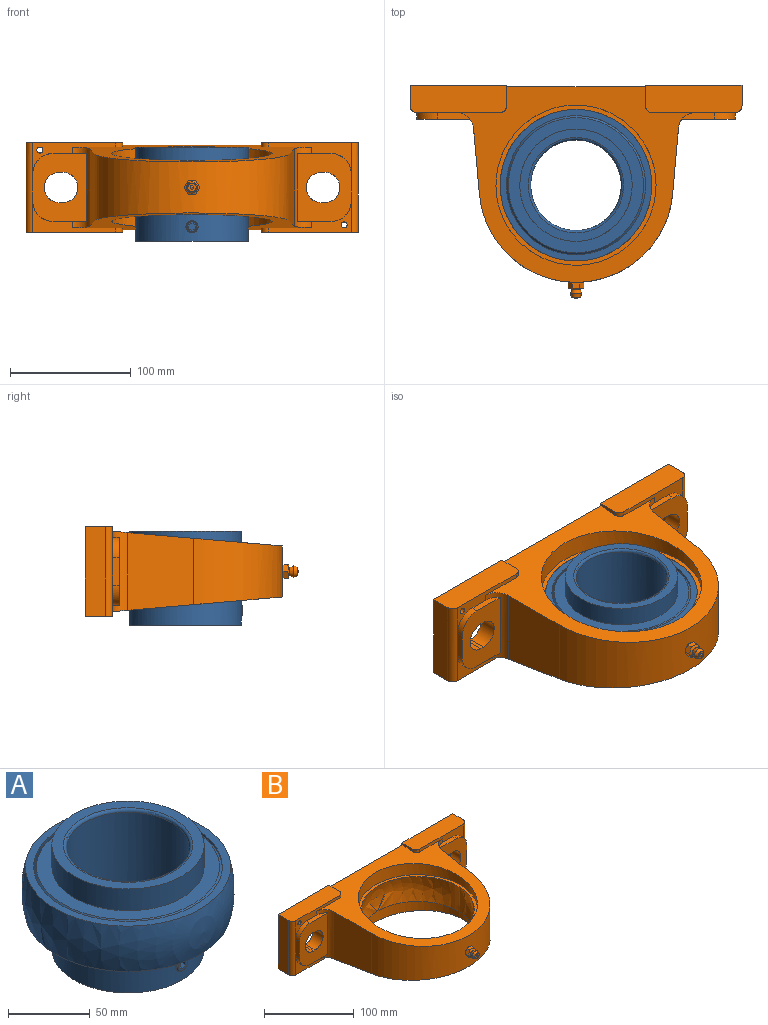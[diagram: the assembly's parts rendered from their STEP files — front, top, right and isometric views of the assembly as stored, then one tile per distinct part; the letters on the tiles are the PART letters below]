
ASSEMBLY  parts=2 mates=1
PART A: 143 faces, bbox 127.1x129.4x131.6 mm
  f0: plane 7.1x6.16mm, normal (0.87,0.5,0), area 38.5mm2, adj f1
  f1: cone r=1.71mm half-angle=45deg, axis (0.87,0.5,0), area 56.6mm2, adj f0,f2
  f2: cylinder r=5mm len=10.05mm, axis (0.87,0.5,0), area 79.3mm2, adj f1,f3
  f3: cylinder r=37.5mm len=75mm, axis (0,0,1), area 17220.6mm2, adj f2,f4,f139,f142
  f4: torus R=39.5mm, axis (0,0,-1), area 754.6mm2, adj f3,f5
  f5: plane 93.01x93.01mm, normal (0,0,-1), area 1887mm2, adj f4,f6
  f6: cylinder r=46.5mm len=93mm, axis (0,0,-1), area 7783.3mm2, adj f5,f7,f105,f106,f107,f108,f109,f110
  f7: sphere r=8.34mm, area 847.9mm2, adj f6,f8,f9,f10,f53,f54,f55,f56
  f8: torus R=51.49mm, axis (0,0,1), area 160.7mm2, adj f7,f9,f95,f106
  f9: torus R=51.49mm, axis (0,0,1), area 160.7mm2, adj f7,f8,f10,f106
  f10: cylinder r=56.49mm len=112.98mm, axis (0,0,1), area 2460.6mm2, adj f7,f9,f11,f13,f15,f17,f19,f21
  f11: torus R=51.49mm, axis (0,0,1), area 160.8mm2, adj f10,f12,f118,f120
  f12: torus R=51.49mm, axis (0,0,1), area 160.7mm2, adj f11,f95,f118,f120
  f13: torus R=51.49mm, axis (0,0,1), area 160.7mm2, adj f10,f14,f116,f118
  f14: torus R=51.49mm, axis (0,0,1), area 160.7mm2, adj f13,f95,f116,f118
  f15: torus R=51.49mm, axis (0,0,1), area 160.7mm2, adj f10,f16,f114,f116
  f16: torus R=51.49mm, axis (0,0,1), area 160.7mm2, adj f15,f95,f114,f116
  f17: torus R=51.49mm, axis (0,0,1), area 160.7mm2, adj f10,f18,f112,f114
  f18: torus R=51.49mm, axis (0,0,1), area 160.7mm2, adj f17,f95,f112,f114
  f19: torus R=51.49mm, axis (0,0,1), area 160.7mm2, adj f10,f20,f110,f112
  f20: torus R=51.49mm, axis (0,0,1), area 160.7mm2, adj f19,f95,f110,f112
  f21: torus R=51.49mm, axis (0,0,1), area 81.7mm2, adj f10,f22,f24,f110
  f22: torus R=51.49mm, axis (0,0,1), area 81.7mm2, adj f21,f23,f95,f110
  f23: torus R=51.49mm, axis (0,0,1), area 78.9mm2, adj f22,f24,f95,f108
  f24: torus R=51.49mm, axis (0,0,1), area 79mm2, adj f10,f21,f23,f108
  f25: torus R=51.49mm, axis (0,0,1), area 160.7mm2, adj f10,f26,f106,f108
  f26: torus R=51.49mm, axis (0,0,1), area 160.7mm2, adj f25,f95,f106,f108
  f27: torus R=51.49mm, axis (0,0,1), area 160.7mm2, adj f10,f28,f135,f137
  f28: torus R=51.49mm, axis (0,0,1), area 160.7mm2, adj f27,f95,f135,f137
  f29: torus R=51.49mm, axis (0,0,1), area 160.7mm2, adj f10,f30,f133,f135
  f30: torus R=51.49mm, axis (0,0,1), area 160.7mm2, adj f29,f95,f133,f135
  f31: torus R=51.49mm, axis (0,0,1), area 160.7mm2, adj f10,f32,f131,f133
  f32: torus R=51.49mm, axis (0,0,1), area 160.7mm2, adj f31,f95,f131,f133
  f33: torus R=51.49mm, axis (0,0,1), area 160.7mm2, adj f10,f34,f129,f131
  f34: torus R=51.49mm, axis (0,0,1), area 160.7mm2, adj f33,f95,f129,f131
  f35: torus R=51.49mm, axis (0,0,1), area 160.7mm2, adj f10,f36,f127,f129
  f36: torus R=51.49mm, axis (0,0,1), area 160.7mm2, adj f35,f95,f127,f129
  f37: torus R=51.49mm, axis (0,0,1), area 160.7mm2, adj f10,f38,f124,f127
  f38: torus R=51.49mm, axis (0,0,1), area 160.7mm2, adj f37,f95,f124,f127
  f39: torus R=51.49mm, axis (0,0,1), area 160.8mm2, adj f10,f40,f122,f124
  f40: torus R=51.49mm, axis (0,0,1), area 160.7mm2, adj f39,f95,f122,f124
  f41: torus R=51.49mm, axis (0,0,1), area 160.8mm2, adj f10,f42,f120,f122
  f42: torus R=51.49mm, axis (0,0,1), area 160.7mm2, adj f41,f95,f120,f122
  f43: cylinder r=0.87mm len=9.02mm, axis (0,-0.97,0.26), area 45.2mm2, adj f10,f44
  f44: sphere r=65mm, area 19597mm2, adj f43,f45
  f45: plane 125.48x125.48mm, normal (0,0,1), area 1907.7mm2, adj f44,f46
  f46: cylinder r=57.62mm len=115.24mm, axis (0,0,1), area 611.8mm2, adj f45,f47
  f47: cone r=55.93mm half-angle=45deg, axis (0,0,1), area 852.6mm2, adj f46,f48
  f48: plane 113.5x113.5mm, normal (0,0,1), area 3025.4mm2, adj f47,f49
  f49: cylinder r=46.51mm len=93.02mm, axis (0,0,-1), area 990.7mm2, adj f48,f50
  f50: plane 115.25x115.25mm, normal (0,0,-1), area 3627.1mm2, adj f49,f51
  f51: cylinder r=57.62mm len=115.24mm, axis (0,0,1), area 3.6mm2, adj f50,f52
  f52: plane 115.25x115.25mm, normal (0,0,1), area 412mm2, adj f10,f51
  f53: torus R=51.49mm, axis (0,0,1), area 160.7mm2, adj f7,f10,f54,f137
  f54: torus R=51.49mm, axis (0,0,1), area 160.7mm2, adj f7,f53,f95,f137
  f55: torus R=51.49mm, axis (0,0,1), area 120.6mm2, adj f7,f56,f137,f138
  f56: cylinder r=46.5mm len=93mm, axis (0,0,-1), area 10888.8mm2, adj f7,f55,f57,f67,f68,f69,f70,f71
  f57: cylinder r=5mm len=10mm, axis (-0.87,-0.5,0), area 4.9mm2, adj f56,f58
  f58: cone r=2.14mm half-angle=45deg, axis (-0.87,-0.5,0), area 37.1mm2, adj f57,f59
  f59: plane 8.28x7.19mm, normal (-0.87,-0.5,0), area 30.7mm2, adj f58,f60,f62,f63,f64,f65,f66
  f60: plane 5.58x4.67mm, normal (-0.25,0.43,0.87), area 14.4mm2, adj f59,f61,f62,f66
  f61: plane 5.77x4.33mm, normal (-0.87,-0.5,0), area 21.7mm2, adj f60,f62,f63,f64,f65,f66
  f62: plane 5.58x4.67mm, normal (0.25,-0.43,0.87), area 14.4mm2, adj f59,f60,f61,f63
  f63: plane 4.33x2.89mm, normal (0.5,-0.87,0), area 14.4mm2, adj f59,f61,f62,f64
  f64: plane 5.58x4.67mm, normal (0.25,-0.43,-0.87), area 14.4mm2, adj f59,f61,f63,f65
  f65: plane 5.58x4.67mm, normal (-0.25,0.43,-0.87), area 14.4mm2, adj f59,f61,f64,f66
  f66: plane 4.33x2.89mm, normal (-0.5,0.87,0), area 14.4mm2, adj f59,f60,f61,f65
  f67: torus R=51.49mm, axis (0,0,1), area 120.6mm2, adj f56,f118,f119,f120
  f68: torus R=51.49mm, axis (0,0,1), area 120.6mm2, adj f56,f116,f117,f118
  f69: torus R=51.49mm, axis (0,0,1), area 120.6mm2, adj f56,f114,f115,f116
  f70: torus R=51.49mm, axis (0,0,1), area 120.6mm2, adj f56,f112,f113,f114
  f71: torus R=51.49mm, axis (0,0,1), area 120.6mm2, adj f56,f110,f111,f112
  f72: torus R=51.49mm, axis (0,0,1), area 120.6mm2, adj f56,f108,f109,f110
  f73: torus R=51.49mm, axis (0,0,1), area 120.6mm2, adj f56,f106,f107,f108
  f74: torus R=51.49mm, axis (0,0,1), area 120.6mm2, adj f56,f135,f136,f137
  f75: torus R=51.49mm, axis (0,0,1), area 120.6mm2, adj f56,f133,f134,f135
  f76: torus R=51.49mm, axis (0,0,1), area 120.6mm2, adj f56,f131,f132,f133
  f77: torus R=51.49mm, axis (0,0,1), area 120.6mm2, adj f56,f129,f130,f131
  f78: torus R=51.49mm, axis (0,0,1), area 120.6mm2, adj f56,f127,f128,f129
  f79: torus R=51.49mm, axis (0,0,1), area 59.1mm2, adj f56,f80,f126,f127
  f80: torus R=51.49mm, axis (0,0,1), area 61.5mm2, adj f56,f79,f124,f125
  f81: torus R=51.49mm, axis (0,0,1), area 120.6mm2, adj f56,f122,f123,f124
  f82: torus R=51.49mm, axis (0,0,1), area 120.6mm2, adj f56,f120,f121,f122
  f83: plane 93.01x93.01mm, normal (0,0,1), area 1887mm2, adj f56,f142
  f84: cylinder r=5mm len=10mm, axis (0,1,0), area 4.9mm2, adj f56,f85
  f85: cone r=4.08mm half-angle=45deg, axis (0,1,0), area 37.1mm2, adj f84,f86
  f86: plane 8.28x8.28mm, normal (0,1,0), area 30.7mm2, adj f85,f87,f89,f90,f91,f92,f93
  f87: plane 5x2.5mm, normal (0.5,0,0.87), area 14.4mm2, adj f86,f88,f89,f93
  f88: plane 5.77x5mm, normal (0,1,0), area 21.7mm2, adj f87,f89,f90,f91,f92,f93
  f89: plane 5x2.5mm, normal (-0.5,0,0.87), area 14.4mm2, adj f86,f87,f88,f90
  f90: plane 5x2.89mm, normal (-1,0,0), area 14.4mm2, adj f86,f88,f89,f91
  f91: plane 5x2.5mm, normal (-0.5,0,-0.87), area 14.4mm2, adj f86,f88,f90,f92
  f92: plane 5x2.5mm, normal (0.5,0,-0.87), area 14.4mm2, adj f86,f88,f91,f93
  f93: plane 5x2.89mm, normal (1,0,0), area 14.4mm2, adj f86,f87,f88,f92
  f94: torus R=51.49mm, axis (0,0,1), area 120.6mm2, adj f7,f56,f105,f106
  f95: cylinder r=56.49mm len=112.98mm, axis (0,0,1), area 2463.2mm2, adj f7,f8,f12,f14,f16,f18,f20,f22
  f96: plane 115.25x115.25mm, normal (0,0,-1), area 397.7mm2, adj f95,f97
  f97: cylinder r=57.62mm len=115.24mm, axis (0,0,1), area 3.6mm2, adj f96,f98
  f98: plane 116.6x116.6mm, normal (0,0,1), area 3638.6mm2, adj f97,f99
  f99: cylinder r=46.51mm len=93.02mm, axis (0,0,1), area 990.7mm2, adj f98,f100
  f100: plane 113.5x113.5mm, normal (0,0,-1), area 3025.4mm2, adj f99,f101
  f101: cone r=55.93mm half-angle=45deg, axis (0,0,-1), area 852.6mm2, adj f100,f102
  f102: cylinder r=57.62mm len=115.24mm, axis (0,0,1), area 611.8mm2, adj f101,f103
  f103: plane 125.48x125.48mm, normal (0,0,-1), area 1909mm2, adj f102,f104
  f104: sphere r=65mm, area 19599.5mm2, adj f103
  f105: torus R=51.49mm, axis (0,0,1), area 120.6mm2, adj f6,f7,f94,f106
  f106: sphere r=8.34mm, area 847.9mm2, adj f6,f8,f9,f10,f25,f26,f56,f73
  f107: torus R=51.49mm, axis (0,0,1), area 120.6mm2, adj f6,f73,f106,f108
  f108: sphere r=8.34mm, area 847.9mm2, adj f6,f10,f23,f24,f25,f26,f56,f72
  f109: torus R=51.49mm, axis (0,0,1), area 120.6mm2, adj f6,f72,f108,f110
  f110: sphere r=8.34mm, area 847.9mm2, adj f6,f10,f19,f20,f21,f22,f56,f71
  f111: torus R=51.49mm, axis (0,0,1), area 120.6mm2, adj f6,f71,f110,f112
  f112: sphere r=8.34mm, area 847.9mm2, adj f6,f10,f17,f18,f19,f20,f56,f70
  f113: torus R=51.49mm, axis (0,0,1), area 120.6mm2, adj f6,f70,f112,f114
  f114: sphere r=8.34mm, area 847.9mm2, adj f6,f10,f15,f16,f17,f18,f56,f69
  f115: torus R=51.49mm, axis (0,0,1), area 120.6mm2, adj f6,f69,f114,f116
  f116: sphere r=8.34mm, area 847.9mm2, adj f6,f10,f13,f14,f15,f16,f56,f68
  f117: torus R=51.49mm, axis (0,0,1), area 120.6mm2, adj f6,f68,f116,f118
  f118: sphere r=8.34mm, area 847.9mm2, adj f6,f10,f11,f12,f13,f14,f56,f67
  f119: torus R=51.49mm, axis (0,0,1), area 120.6mm2, adj f6,f67,f118,f120
  f120: sphere r=8.34mm, area 847.9mm2, adj f6,f10,f11,f12,f41,f42,f56,f67
  f121: torus R=51.49mm, axis (0,0,1), area 120.6mm2, adj f6,f82,f120,f122
  f122: sphere r=8.34mm, area 847.9mm2, adj f6,f10,f39,f40,f41,f42,f56,f81
  f123: torus R=51.49mm, axis (0,0,1), area 120.6mm2, adj f6,f81,f122,f124
  f124: sphere r=8.34mm, area 847.9mm2, adj f6,f10,f37,f38,f39,f40,f56,f80
  f125: torus R=51.49mm, axis (0,0,1), area 61.5mm2, adj f6,f80,f124,f126
  f126: torus R=51.49mm, axis (0,0,1), area 59.1mm2, adj f6,f79,f125,f127
  f127: sphere r=8.34mm, area 847.9mm2, adj f6,f10,f35,f36,f37,f38,f56,f78
  f128: torus R=51.49mm, axis (0,0,1), area 120.6mm2, adj f6,f78,f127,f129
  f129: sphere r=8.34mm, area 847.9mm2, adj f6,f10,f33,f34,f35,f36,f56,f77
  f130: torus R=51.49mm, axis (0,0,1), area 120.6mm2, adj f6,f77,f129,f131
  f131: sphere r=8.34mm, area 847.9mm2, adj f6,f10,f31,f32,f33,f34,f56,f76
  f132: torus R=51.49mm, axis (0,0,1), area 120.6mm2, adj f6,f76,f131,f133
  f133: sphere r=8.34mm, area 847.9mm2, adj f6,f10,f29,f30,f31,f32,f56,f75
  f134: torus R=51.49mm, axis (0,0,1), area 120.6mm2, adj f6,f75,f133,f135
  f135: sphere r=8.34mm, area 847.9mm2, adj f6,f10,f27,f28,f29,f30,f56,f74
  f136: torus R=51.49mm, axis (0,0,1), area 120.6mm2, adj f6,f74,f135,f137
  f137: sphere r=8.34mm, area 847.9mm2, adj f6,f10,f27,f28,f53,f54,f55,f56
  f138: torus R=51.49mm, axis (0,0,1), area 120.6mm2, adj f6,f7,f55,f137
  f139: cylinder r=5mm len=10mm, axis (0,-1,0), area 79.3mm2, adj f3,f140
  f140: cone r=3.5mm half-angle=45deg, axis (0,-1,0), area 56.6mm2, adj f139,f141
  f141: plane 7.1x7.1mm, normal (0,-1,0), area 38.5mm2, adj f140
  f142: torus R=39.5mm, axis (0,0,-1), area 754.6mm2, adj f3,f83
PART B: 85 faces, bbox 315.1x216.6x170.1 mm
  f0: plane 65.39x49.89mm, normal (0,1,0), area 2651.8mm2, adj f8,f9,f10,f11,f13,f14,f15,f16
  f1: plane 65.39x49.89mm, normal (0,1,0), area 2651.8mm2, adj f3,f4,f5,f6,f18,f19,f20,f21
  f2: sphere r=65.01mm, area 12961.5mm2, adj f24,f27
  f3: plane 49.5x12.6mm, normal (1,0,0), area 623.7mm2, adj f1,f4,f6,f31
  f4: plane 65x12.6mm, normal (0,0,1), area 819mm2, adj f1,f3,f5,f31
  f5: plane 49.5x12.6mm, normal (-1,0,0), area 623.7mm2, adj f1,f4,f6,f31
  f6: plane 65x12.6mm, normal (0,0,-1), area 819mm2, adj f1,f3,f5,f31
  f7: plane 74x16.8mm, normal (1,0,0), area 1243.2mm2, adj f29,f30,f31,f32
  f8: plane 49.5x12.6mm, normal (1,0,0), area 623.7mm2, adj f0,f9,f11,f33
  f9: plane 65x12.6mm, normal (0,0,1), area 819mm2, adj f0,f8,f10,f33
  f10: plane 49.5x12.6mm, normal (-1,0,0), area 623.7mm2, adj f0,f9,f11,f33
  f11: plane 65x12.6mm, normal (0,0,-1), area 819mm2, adj f0,f8,f10,f33
  f12: plane 74x16.8mm, normal (-1,0,0), area 1243.2mm2, adj f33,f34,f35,f36
  f13: plane 15.4x3mm, normal (0,0,1), area 46.2mm2, adj f0,f14,f16,f39
  f14: cylinder r=12.5mm len=25mm, axis (0,-1,0), area 604.8mm2, adj f0,f13,f15,f39
  f15: plane 15.4x3mm, normal (0,0,-1), area 46.2mm2, adj f0,f14,f16,f39
  f16: cylinder r=12.5mm len=25mm, axis (0,-1,0), area 604.8mm2, adj f0,f13,f15,f39
  f17: plane 22.52x5.6mm, normal (-1,0,0), area 126.1mm2, adj f26,f36,f37,f39
  f18: plane 15.4x3mm, normal (0,0,1), area 46.2mm2, adj f1,f19,f21,f42
  f19: cylinder r=12.5mm len=25mm, axis (0,-1,0), area 604.8mm2, adj f1,f18,f20,f42
  f20: plane 15.4x3mm, normal (0,0,-1), area 46.2mm2, adj f1,f19,f21,f42
  f21: cylinder r=12.5mm len=25mm, axis (0,-1,0), area 604.8mm2, adj f1,f18,f20,f42
  f22: plane 22.52x5.6mm, normal (1,0,0), area 126.1mm2, adj f25,f28,f29,f42
  f23: sphere r=2.11mm, area 8.9mm2, adj f44
  f24: plane 172.74x172.74mm, normal (0,0,-1), area 1506mm2, adj f2,f45,f46
  f25: cylinder r=16.89mm len=16.89mm, axis (0,1,0), area 148.6mm2, adj f22,f41,f42,f47
  f26: cylinder r=16.89mm len=16.89mm, axis (0,1,0), area 148.6mm2, adj f17,f39,f40,f48
  f27: plane 172.74x172.74mm, normal (0,0,1), area 1506mm2, adj f2,f51
  f28: cylinder r=16.89mm len=16.89mm, axis (0,1,0), area 148.6mm2, adj f22,f42,f43,f52
  f29: cylinder r=5.6mm len=74mm, axis (0,0,1), area 650.9mm2, adj f7,f22,f30,f32,f47,f52
  f30: plane 80.35x22.75mm, normal (0,0,1), area 1778.7mm2, adj f7,f29,f31,f52,f53,f54
  f31: plane 80x74mm, normal (0,1,0), area 2682.9mm2, adj f3,f4,f5,f6,f7,f30,f32,f54
  f32: plane 80.35x22.75mm, normal (0,0,-1), area 1778.5mm2, adj f7,f29,f31,f47,f50,f54
  f33: plane 80x74mm, normal (0,1,0), area 2682.9mm2, adj f8,f9,f10,f11,f12,f34,f35,f56
  f34: plane 80.35x22.75mm, normal (0,0,-1), area 1778.7mm2, adj f12,f33,f36,f48,f49,f56
  f35: plane 80.35x22.75mm, normal (0,0,1), area 1778.5mm2, adj f12,f33,f36,f56,f57,f58
  f36: cylinder r=5.6mm len=74mm, axis (0,0,1), area 650.9mm2, adj f12,f17,f34,f35,f48,f58
  f37: cylinder r=16.89mm len=16.89mm, axis (0,1,0), area 148.6mm2, adj f17,f38,f39,f58
  f38: plane 27.73x5.93mm, normal (0,0,1), area 134.6mm2, adj f37,f39,f58,f59
  f39: plane 56.3x44.3mm, normal (0,-1,0), area 1805.6mm2, adj f13,f14,f15,f16,f17,f26,f37,f38
  f40: plane 27.74x5.93mm, normal (0,0,-1), area 134.6mm2, adj f26,f39,f48,f59
  f41: plane 27.65x5.84mm, normal (0,0,-1), area 134.6mm2, adj f25,f42,f47,f61
  f42: plane 56.3x44.3mm, normal (0,-1,0), area 1805.6mm2, adj f18,f19,f20,f21,f22,f25,f28,f41
  f43: plane 27.65x5.84mm, normal (0,0,1), area 134.6mm2, adj f28,f42,f52,f61
  f44: plane 7.06x7.06mm, normal (0,-1,0), area 30.6mm2, adj f23,f62
  f45: cylinder r=66.31mm len=132.62mm, axis (0,0,1), area 3063mm2, adj f24,f46,f63
  f46: cylinder r=66.31mm len=132.62mm, axis (0,0,1), area 1706.5mm2, adj f24,f45,f63
  f47: plane 68.8x25.74mm, normal (0,-1,0), area 468.3mm2, adj f25,f29,f32,f41,f50,f61,f63,f84
  f48: plane 68.8x25.74mm, normal (0,-1,0), area 487.9mm2, adj f26,f34,f36,f40,f49,f59,f63
  f49: cylinder r=5.6mm len=5.6mm, axis (0,0,1), area 30.8mm2, adj f34,f48,f56,f63
  f50: cylinder r=5.6mm len=5.6mm, axis (0,0,-1), area 30.8mm2, adj f32,f47,f54,f63
  f51: cylinder r=66.31mm len=132.62mm, axis (0,0,-1), area 4442.1mm2, adj f27,f65
  f52: plane 68.8x25.74mm, normal (0,-1,0), area 487.9mm2, adj f28,f29,f30,f43,f53,f61,f65
  f53: cylinder r=5.6mm len=5.6mm, axis (0,0,-1), area 30.8mm2, adj f30,f52,f54,f65
  f54: plane 74x16.8mm, normal (-1,0,0), area 164mm2, adj f30,f31,f32,f50,f53,f55,f63,f65
  f55: plane 115x70.18mm, normal (0,1,0), area 8070.8mm2, adj f54,f56,f63,f65
  f56: plane 74x16.8mm, normal (1,0,0), area 164mm2, adj f33,f34,f35,f49,f55,f57,f63,f65
  f57: cylinder r=5.6mm len=5.6mm, axis (0,0,1), area 30.8mm2, adj f35,f56,f58,f65
  f58: plane 68.8x25.74mm, normal (0,-1,0), area 468.3mm2, adj f35,f36,f37,f38,f57,f59,f65,f83
  f59: cylinder r=14mm len=66.51mm, axis (0,0,-1), area 627.5mm2, adj f38,f39,f40,f48,f58,f60,f63,f65
  f60: plane 64.3x54.43mm, normal (-1,-0.09,0), area 3256.2mm2, adj f59,f63,f65,f67
  f61: cylinder r=14mm len=66.51mm, axis (0,0,-1), area 627.5mm2, adj f41,f42,f43,f47,f52,f63,f64,f65
  f62: cone r=4.62mm half-angle=20deg, axis (0,1,0), area 84.4mm2, adj f44,f66
  f63: plane 205.48x169.85mm, normal (0,-0.09,-1), area 8924.4mm2, adj f45,f46,f47,f48,f49,f50,f54,f55
  f64: plane 64.3x54.43mm, normal (1,-0.09,0), area 3256.2mm2, adj f61,f63,f65,f67
  f65: plane 205.48x169.85mm, normal (0,-0.09,1), area 8912mm2, adj f51,f52,f53,f54,f55,f56,f57,f58
  f66: cone r=4.62mm half-angle=15deg, axis (0,-1,0), area 95.9mm2, adj f62,f71
  f67: cylinder r=80.4mm len=160.19mm, axis (0,0,1), area 12121.7mm2, adj f60,f63,f64,f65,f74
  f68: plane 7.55x7.01mm, normal (0.87,0,-0.5), area 30.1mm2, adj f69,f71,f72,f77,f78
  f69: plane 8.41x7.01mm, normal (0,0,-1), area 30.1mm2, adj f68,f70,f71,f78,f79
  f70: plane 7.55x7.01mm, normal (-0.87,0,-0.5), area 30.1mm2, adj f69,f71,f73,f75,f79
  f71: cone r=3.66mm half-angle=60deg, axis (0,1,0), area 101mm2, adj f66,f68,f69,f70,f72,f73,f80
  f72: plane 7.55x7.01mm, normal (0.87,0,0.5), area 30.1mm2, adj f68,f71,f76,f77,f80
  f73: plane 7.55x7.01mm, normal (-0.87,0,0.5), area 30.1mm2, adj f70,f71,f75,f80,f82
  f74: cylinder r=3.98mm len=7.96mm, axis (0,1,0), area 1.5mm2, adj f67,f81
  f75: cone r=5.56mm half-angle=60deg, axis (0,-1,0), area 3mm2, adj f70,f73,f81
  f76: cone r=5.56mm half-angle=60deg, axis (0,-1,0), area 3mm2, adj f72,f80,f81
  f77: cone r=5.56mm half-angle=60deg, axis (0,-1,0), area 3mm2, adj f68,f72,f81
  f78: cone r=5.56mm half-angle=60deg, axis (0,-1,0), area 2.6mm2, adj f68,f69,f81
  f79: cone r=5.56mm half-angle=60deg, axis (0,-1,0), area 3mm2, adj f69,f70,f81
  f80: plane 8.41x7.01mm, normal (0,0,1), area 30.1mm2, adj f71,f72,f73,f76,f82
  f81: plane 11.3x11.3mm, normal (0,1,0), area 47.5mm2, adj f74,f75,f76,f77,f78,f79,f82
  f82: cone r=5.56mm half-angle=60deg, axis (0,-1,0), area 2.6mm2, adj f73,f80,f81
  f83: cylinder r=2.5mm len=22.4mm, axis (0,-1,0), area 351.9mm2, adj f33,f58
  f84: cylinder r=2.5mm len=22.4mm, axis (0,-1,0), area 351.9mm2, adj f31,f47
PLACE A at identity
PLACE B at identity
MATE fastened A.f121 <-> B.f45  axis (0,0,-1) through (108.5,-82.6,-44.5)mm
